# Revit family: QF_ELECTROLUXPROFESSIONAL_1LSN26_WH6-8_S
name_source: partatom
category: Attrezzature speciali
units: mm (PartAtom-declared; Revit-internal decimal feet)

## family parameters
Basato su piano di lavoro = No
Condiviso = No
Punto di calcolo locali = No
Quota connettore circolare = Usa diametro
Sempre verticale = Sì
Taglio con vuoti quando caricato = No
Tipo di parte = Normale

## types (1)
- 9867630188
    Cycle = 50 Hz
    Depth Actual = 721 mm
    Descrizione = WASHER WH6-8 8KG STEAM 220-240/50/1N COMPASS PRO 6G01 ML 2xWATER POWDER+5xLIQ. VALV.OPEN SILVER 2.I/O DISCON. STOP
    Gas KW = 0
    Height Actual = 1132 mm
    Item Number = 1L8261
    Latent Heat Output = 0.0
    Length Actual = 720 mm  [stored 2.3622 ft]
    Modello = WH6-8
    Phase = 1
    Produttore = Electrolux Professional
    Prospetto di default = 0 mm  [stored 0 ft]
    Sensible Heat Output = 0.0
    Steam Pounds per Hour = 0
    URL = www.electroluxprofessional.com
    Volts = 240 V
    Watts = 1000 W
    Weight = 158

note: [stored X ft] marks values corroborated as IEEE doubles in the binary element streams (Revit-internal decimal feet)

## geometry (parser evidence)
native form markers: Blend x6
no freeform markers — native parametric forms only
